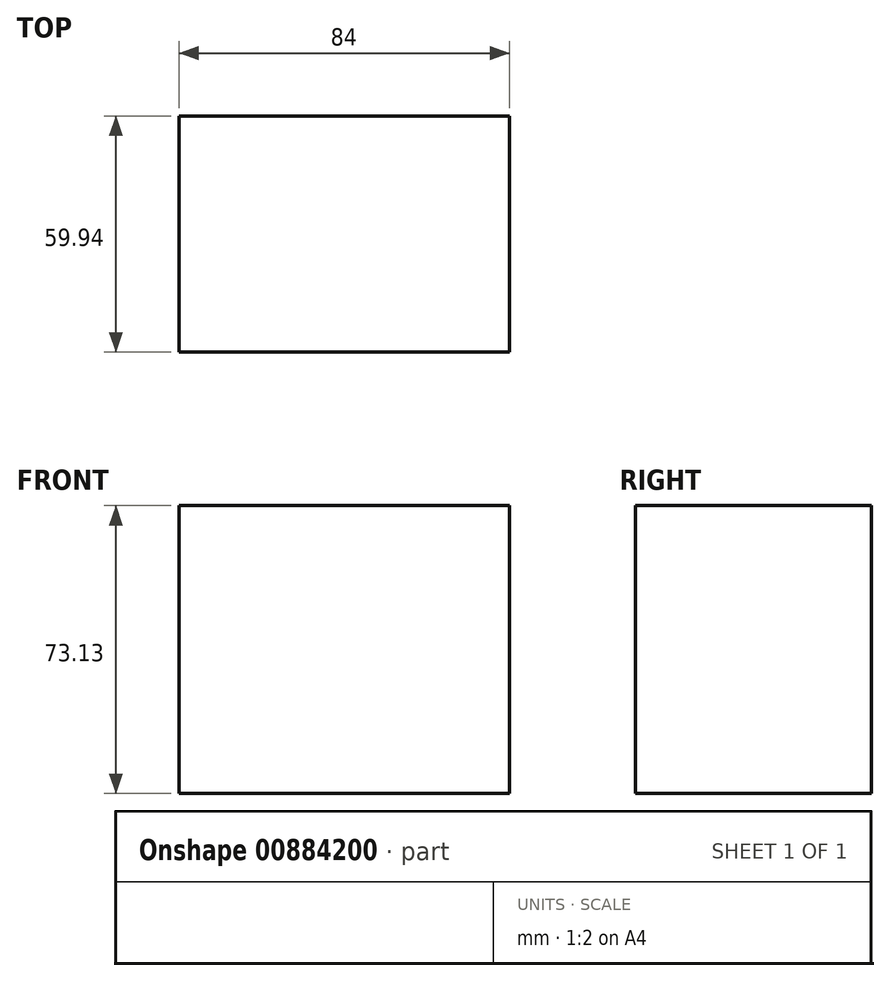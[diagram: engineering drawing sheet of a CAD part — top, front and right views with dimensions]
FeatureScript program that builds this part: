
annotation { "Feature Type Name" : "Feature", "Feature Type Description" : "" }
export const myFeature = defineFeature(function(context is Context, id is Id, definition is map)
    precondition{}
    {
        {
            var Q0;
            Q0=qCreatedBy(makeId("Front.planeOp"),FACE);
            var sketch = newSketch(context, id + "F0", { "sketchPlane" : qUnion([Q0])});
            skLineSegment(sketch, "E0.bottom", {"start": v(-37.45, -21.59) * mm, "end": v(46.55, -21.59) * mm});
            skLineSegment(sketch, "E0.top", {"start": v(-37.45, 51.54) * mm, "end": v(46.55, 51.54) * mm});
            skLineSegment(sketch, "E0.left", {"start": v(-37.45, -21.59) * mm, "end": v(-37.45, 51.54) * mm});
            skLineSegment(sketch, "E0.right", {"start": v(46.55, -21.59) * mm, "end": v(46.55, 51.54) * mm});
            skSolve(sketch);
        }
        {
            var Q0;
            Q0=makeQuery(id+"F0.imprint","IMPRINT",FACE,{"disambiguationData":[TD([[makeQuery(id+"F0.imprint","IMPRINT",EDGE,{"derivedFrom":sQuery(id+"F0.wireOp",EDGE,"E0.bottom")}),1.0]])]});
            var sketch = newSketch(context, id + "F1", { "sketchPlane" : qUnion([Q0])});
            skSolve(sketch);
        }
        {
            var Q0;
            Q0 = qSketchRegion(id + "F1", true);
            var Q1;
            Q1=makeQuery(id+"F0.imprint","IMPRINT",FACE,{"disambiguationData":[TD([[makeQuery(id+"F0.imprint","IMPRINT",EDGE,{"derivedFrom":sQuery(id+"F0.wireOp",EDGE,"E0.bottom")}),1.0]])]});
            var Q2;
            Q2=makeQuery(id+"F1.imprint","IMPRINT",FACE,{"disambiguationData":[TD([[makeQuery(id+"F1.imprint","IMPRINT",EDGE,{"derivedFrom":makeQuery(id+"F0.imprint","IMPRINT",EDGE,{"derivedFrom":sQuery(id+"F0.wireOp",EDGE,"E0.bottom")})}),1.0]])]});
            extrude(context, id + "F2", {"entities" : qUnion([Q0, Q1, Q2]), "depth" : 59.94 * mm, "offsetDistance" : 25.4 * mm});
        }
    });
